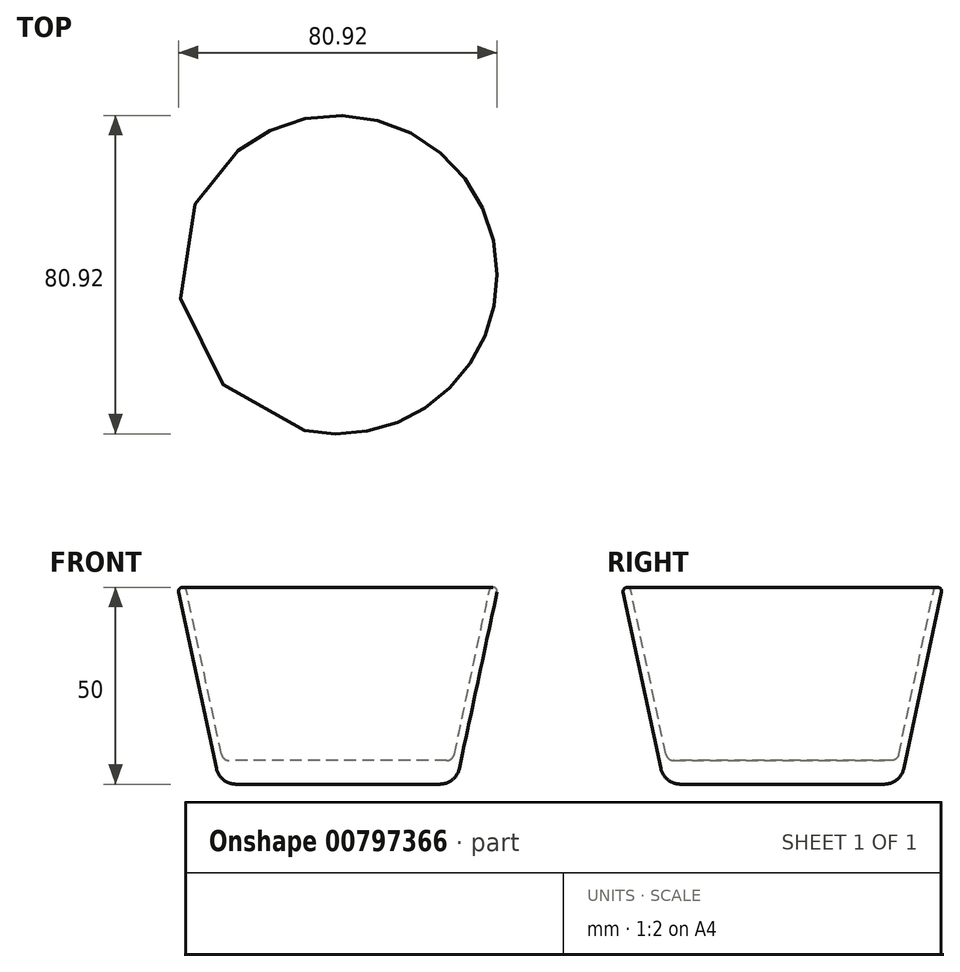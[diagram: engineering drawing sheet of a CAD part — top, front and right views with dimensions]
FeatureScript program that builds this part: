
annotation { "Feature Type Name" : "Feature", "Feature Type Description" : "" }
export const myFeature = defineFeature(function(context is Context, id is Id, definition is map)
    precondition{}
    {
        {
            var Q0;
            Q0=qCreatedBy(makeId("Front.planeOp"),FACE);
            var sketch = newSketch(context, id + "F0", { "sketchPlane" : qUnion([Q0])});
            skLineSegment(sketch, "E0", {"start": v(0, 0) * mm, "end": v(25.96, 0) * mm});
            skLineSegment(sketch, "E1", {"start": v(30.85, 3.95) * mm, "end": v(40.44, 48.8) * mm});
            skPoint(sketch, "E2.visualSharp", {"position": v(30, 0) * mm});
            skArc(sketch, "E2.filletArc", {"start": v(25.96, 0) * mm, "mid": v(29.1, 1.11) * mm, "end": v(30.85, 3.95) * mm});
            skLineSegment(sketch, "E3.0", {"start": v(29.58, 7.58) * mm, "end": v(38.48, 49.2) * mm});
            skLineSegment(sketch, "E4.0", {"start": v(0, 6) * mm, "end": v(27.62, 6) * mm});
            skArc(sketch, "E5.filletArc", {"start": v(27.62, 6) * mm, "mid": v(28.88, 6.44) * mm, "end": v(29.58, 7.58) * mm});
            skArc(sketch, "E6", {"start": v(40.44, 48.8) * mm, "mid": v(39.67, 49.98) * mm, "end": v(38.48, 49.2) * mm});
            skPoint(sketch, "E6.first.point", {"position": v(38.48, 49.2) * mm});
            skPoint(sketch, "E6.second.point", {"position": v(39.67, 49.98) * mm});
            skPoint(sketch, "E6.third.point", {"position": v(40.44, 48.8) * mm});
            skPoint(sketch, "E7.orphan", {"position": v(40.7, 50) * mm});
            skLineSegment(sketch, "E8", {"start": v(0, 6) * mm, "end": v(0, 0) * mm});
            skSolve(sketch);
        }
        {
            var Q0;
            Q0=makeQuery(id+"F0.imprint","IMPRINT",FACE,{"disambiguationData":[TD([[makeQuery(id+"F0.imprint","IMPRINT",EDGE,{"derivedFrom":sQuery(id+"F0.wireOp",EDGE,"E0")}),1.0]])]});
            var Q1;
            Q1=sQuery(id+"F0.wireOp",EDGE,"E8");
            revolve(context, id + "F1", {"surfaceOperationType" : NewSurfaceOperationType.NEW, "entities" : qUnion([Q0]), "axis" : qUnion([Q1]), "revolveType" : RevolveType.FULL});
        }
    });
